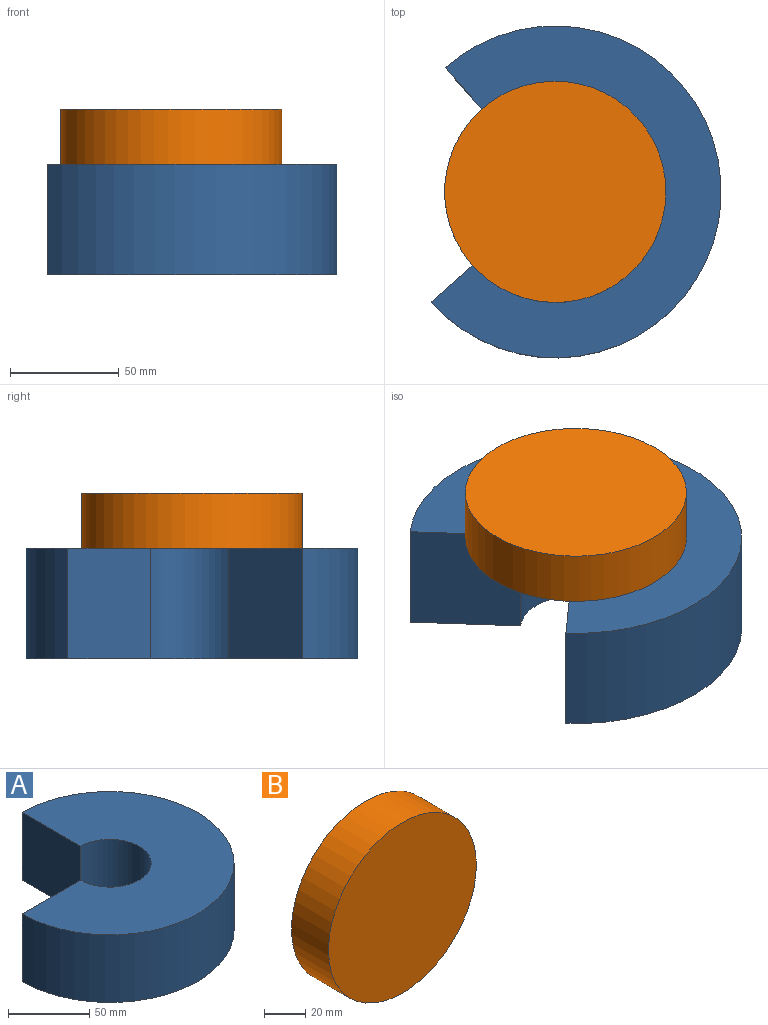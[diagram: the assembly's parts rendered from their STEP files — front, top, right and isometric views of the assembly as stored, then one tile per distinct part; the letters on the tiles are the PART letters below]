
ASSEMBLY  parts=2 mates=1
PART A: 6 faces, bbox 152.4x152.4x50.8 mm
  f0: cylinder r=25.4mm len=50.8mm, axis (0,0,-1), area 6080.5mm2, adj f2,f3,f4,f5
  f1: cylinder r=76.2mm len=152.4mm, axis (0,0,-1), area 18241.5mm2, adj f2,f3,f4,f5
  f2: plane 152.4x152.4mm, normal (0,0,1), area 12161mm2, adj f0,f1,f4,f5
  f3: plane 152.4x152.4mm, normal (0,0,-1), area 12161mm2, adj f0,f1,f4,f5
  f4: plane 50.8x50.8mm, normal (-1,0,0), area 2580.6mm2, adj f0,f1,f2,f3
  f5: plane 50.8x50.8mm, normal (0,1,0), area 2580.6mm2, adj f0,f1,f2,f3
PART B: 3 faces, bbox 101.6x25.4x101.6 mm
  f0: cylinder r=50.8mm len=101.6mm, axis (0,1,0), area 8107.3mm2, adj f1,f2
  f1: plane 101.6x101.6mm, normal (0,-1,0), area 8107.3mm2, adj f0
  f2: plane 101.6x101.6mm, normal (0,1,0), area 8107.3mm2, adj f0
PLACE A rot(axis=(0,0,1),41.5deg) t=(-216.6,-112.65,-6.79)mm
PLACE B rot(axis=(1,0,0),90deg) t=(-216.6,-112.65,69.41)mm fixed
MATE revolute B.f0 <-> A.f0  axis (0,0,-1) through (-216.6,-112.65,44.01)mm
